# Revit family: HRF-S
name_source: partatom
category: Plumbing Fixtures
units: mm (PartAtom-declared; Revit-internal decimal feet)

## family parameters
Always vertical = Yes
Cut with Voids When Loaded = No
OmniClass Number = 23.45.00.00
OmniClass Title = Sanitary, Laundry, and Cleaning Equipment
Part Type = Normal
Room Calculation Point = No
Round Connector Dimension = Use Diameter
Shared = No
Work Plane-Based = No

## types (4) — shared parameters
Activation = Push Button
Apparent Load Phase 1 = 0 VA
Bubbler = Double Bubbler/VR Bubbler
Button Material = Metal - Steel - Stainless - Chrome
CW Connection = Yes
Cooler Depth = 1' - 0 1/4"
Cooler Rim Height = 3' - 3 1/2"
Cooler Width = 1' - 0 1/8"
Description = Water Cooler
HW Connection = No
Manufacturer = Halsey Taylor
Model = HRFS
Orifice Height = 3' - 5 1/8"
Orifice to Rim = 0' - 1 5/8"
Panel Material = Metal - Steel - Stainless - Chrome
Rim Height = 3' - 3 1/2"
Rim to Dispenser = 0' - 6 1/2"
Sanitary Service Size Radius = 0' - 0 5/8"
Specification URL = http://www.halseytaylor.com
Type = Single
URL = http://www.halseytaylor.com
Vent Connection = No
Version = 1.0.0.0
Voltage = 0 V
Volts/Hertz = 115V/60Hz
Wall Plate Material = Metal - Steel - Stainless - Chrome
Waste Connection = Yes
Water Service Flow = 0 GPM
Water Service Size Radius = 0' - 0 1/4"

## per-type parameters (varying)
| type | Basin Material | Freeze Resistan |
| HRF-S | Metal - Steel - Stainless - Chrome | No |
| HRF-S W/FR BOX | Metal - Steel - Stainless - Chrome | Yes |
| HRFG-S BLK BASIN | BLK Marblyte | No |
| HRFG-S GRY BASIN | GRY Marblyte | No |

## geometry (parser evidence)
native form markers: Sweep x8
no freeform markers — native parametric forms only
